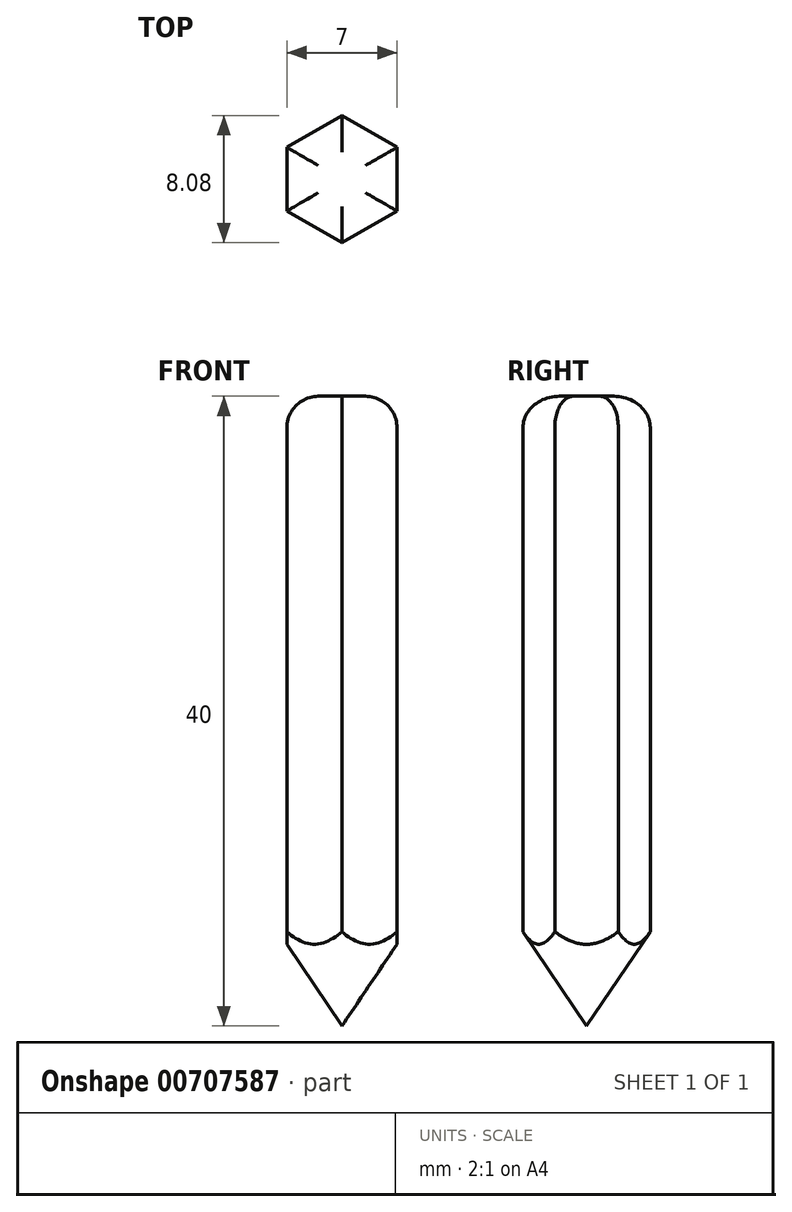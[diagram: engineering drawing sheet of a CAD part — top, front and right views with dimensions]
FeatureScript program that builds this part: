
annotation { "Feature Type Name" : "Feature", "Feature Type Description" : "" }
export const myFeature = defineFeature(function(context is Context, id is Id, definition is map)
    precondition{}
    {
        {
            var Q0;
            Q0=qCreatedBy(makeId("Top.planeOp"),FACE);
            var sketch = newSketch(context, id + "F0", { "sketchPlane" : qUnion([Q0])});
            skCircle(sketch, "E0.cCircle", {"center": v(0, 0) * mm, "radius": 3.5 * mm, "construction": true});
            skLineSegment(sketch, "E0.0", {"start": v(-3.5, -2.02) * mm, "end": v(-3.5, 2.02) * mm});
            skLineSegment(sketch, "E0.1", {"start": v(-3.5, 2.02) * mm, "end": v(0, 4.04) * mm});
            skLineSegment(sketch, "E0.2", {"start": v(0, 4.04) * mm, "end": v(3.5, 2.02) * mm});
            skLineSegment(sketch, "E0.3", {"start": v(3.5, 2.02) * mm, "end": v(3.5, -2.02) * mm});
            skLineSegment(sketch, "E0.4", {"start": v(3.5, -2.02) * mm, "end": v(0, -4.04) * mm});
            skLineSegment(sketch, "E0.5", {"start": v(0, -4.04) * mm, "end": v(-3.5, -2.02) * mm});
            skPoint(sketch, "E0.0.midPoint", {"position": v(-3.5, 0) * mm});
            skSolve(sketch);
        }
        {
            var Q0;
            Q0=makeQuery(id+"F0.imprint","IMPRINT",FACE,{"disambiguationData":[TD([[makeQuery(id+"F0.imprint","IMPRINT",EDGE,{"derivedFrom":sQuery(id+"F0.wireOp",EDGE,"E0.0")}),-1.0]])]});
            extrude(context, id + "F1", {"entities" : qUnion([Q0]), "depth" : 40 * mm, "offsetDistance" : 25 * mm});
        }
        {
            var Q0;
            Q0=makeQuery(id+"F1.opExtrude","CAP_FACE",FACE,{"disambiguationData":[OSD([sQuery(id+"F0.wireOp",EDGE,"E0.0"),sQuery(id+"F0.wireOp",EDGE,"E0.1"),sQuery(id+"F0.wireOp",EDGE,"E0.2"),sQuery(id+"F0.wireOp",EDGE,"E0.3"),sQuery(id+"F0.wireOp",EDGE,"E0.4"),sQuery(id+"F0.wireOp",EDGE,"E0.5")])],"isStart":false});
            fillet(context, id + "F2", {"entities" : qUnion([Q0]), "radius" : 2 * mm, "tangentPropagation" : true, "allowEdgeOverflow" : false});
        }
        {
            var Q0;
            Q0=qCreatedBy(makeId("Right.planeOp"),FACE);
            var sketch = newSketch(context, id + "F3", { "sketchPlane" : qUnion([Q0])});
            skLineSegment(sketch, "E1", {"start": v(0, 0) * mm, "end": v(11.75, 17.42) * mm});
            skLineSegment(sketch, "E2", {"start": v(11.75, 17.42) * mm, "end": v(22.11, 17.42) * mm});
            skLineSegment(sketch, "E3", {"start": v(22.11, 17.42) * mm, "end": v(19.8, -5.38) * mm});
            skLineSegment(sketch, "E4", {"start": v(19.8, -5.38) * mm, "end": v(0, -5.38) * mm});
            skLineSegment(sketch, "E5", {"start": v(0, -5.38) * mm, "end": v(0, 0) * mm});
            skSolve(sketch);
        }
        {
            var Q0;
            Q0=makeQuery(id+"F3.imprint","IMPRINT",FACE,{"disambiguationData":[TD([[makeQuery(id+"F3.imprint","IMPRINT",EDGE,{"derivedFrom":sQuery(id+"F3.wireOp",EDGE,"E1")}),-1.0]])]});
            var Q1;
            Q1=sQuery(id+"F3.wireOp",EDGE,"E5");
            revolve(context, id + "F4", {"operationType" : NewBodyOperationType.REMOVE, "surfaceOperationType" : NewSurfaceOperationType.NEW, "entities" : qUnion([Q0]), "axis" : qUnion([Q1]), "revolveType" : RevolveType.FULL, "oppositeDirection" : true});
        }
    });
